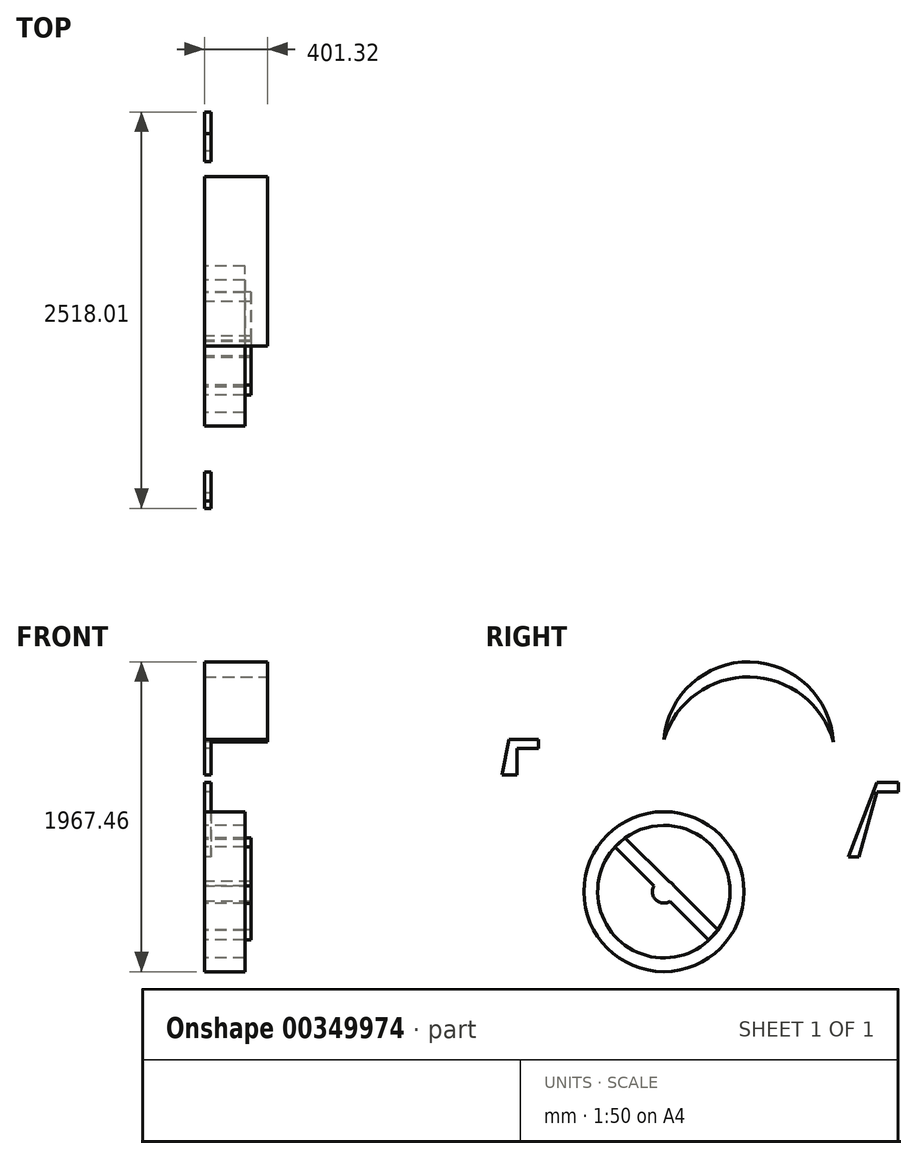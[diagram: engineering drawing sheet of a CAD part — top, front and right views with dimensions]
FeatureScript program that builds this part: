
annotation { "Feature Type Name" : "Feature", "Feature Type Description" : "" }
export const myFeature = defineFeature(function(context is Context, id is Id, definition is map)
    precondition{}
    {
        {
            var Q0;
            Q0=qCreatedBy(makeId("Right.planeOp"),FACE);
            var sketch = newSketch(context, id + "F0", { "sketchPlane" : qUnion([Q0])});
            skCircle(sketch, "E0", {"center": v(0, 0) * mm, "radius": 508 * mm});
            skCircle(sketch, "E1", {"center": v(0, 0) * mm, "radius": 420.64 * mm});
            skSolve(sketch);
        }
        {
            var Q0;
            Q0 = qSketchRegion(id + "F0", true);
            extrude(context, id + "F1", {"entities" : qUnion([Q0]), "depth" : 256.54 * mm});
        }
        {
            var Q0;
            Q0=qCreatedBy(makeId("Right.planeOp"),FACE);
            var sketch = newSketch(context, id + "F2", { "sketchPlane" : qUnion([Q0])});
            skCircle(sketch, "E2", {"center": v(0, 0) * mm, "radius": 73 * mm});
            skLineSegment(sketch, "E3", {"start": v(-310.82, 282.74) * mm, "end": v(282.74, -304.8) * mm});
            skLineSegment(sketch, "E4", {"start": v(282.74, -304.8) * mm, "end": v(343.63, -243.3) * mm});
            skLineSegment(sketch, "E5", {"start": v(343.63, -243.3) * mm, "end": v(-247.6, 341.94) * mm});
            skLineSegment(sketch, "E6", {"start": v(-247.6, 341.94) * mm, "end": v(-310.82, 282.74) * mm});
            skSolve(sketch);
        }
        {
            var Q0;
            Q0 = qSketchRegion(id + "F2", true);
            extrude(context, id + "F3", {"entities" : qUnion([Q0]), "operationType" : NewBodyOperationType.ADD, "depth" : 294.64 * mm});
        }
        {
            var Q0;
            Q0=qCreatedBy(makeId("Right.planeOp"),FACE);
            var sketch = newSketch(context, id + "F4", { "sketchPlane" : qUnion([Q0])});
            skArc(sketch, "E7", {"start": v(1076.69, 949.49) * mm, "mid": v(546.96, 1459.38) * mm, "end": v(0, 968.02) * mm});
            skLineSegment(sketch, "E8", {"start": v(0, 968.02) * mm, "end": v(1076.69, 949.49) * mm});
            skSolve(sketch);
        }
        {
            var Q0;
            Q0 = qSketchRegion(id + "F4", true);
            extrude(context, id + "F5", {"entities" : qUnion([Q0]), "depth" : 401.32 * mm, "offsetDistance" : 25.4 * mm});
        }
        {
            var Q0;
            Q0=makeQuery(id+"F5.opExtrude","CAP_FACE",FACE,{"disambiguationData":[OSD([sQuery(id+"F4.wireOp",EDGE,"E7"),sQuery(id+"F4.wireOp",EDGE,"E8")])],"isStart":false});
            var sketch = newSketch(context, id + "F6", { "sketchPlane" : qUnion([Q0])});
            skArc(sketch, "E9", {"start": v(1076.69, 949.49) * mm, "mid": v(545.32, 1363.83) * mm, "end": v(0, 968.02) * mm});
            skLineSegment(sketch, "E10", {"start": v(0, 968.02) * mm, "end": v(1076.69, 949.49) * mm});
            skSolve(sketch);
        }
        {
            var Q0;
            Q0 = qSketchRegion(id + "F6", true);
            extrude(context, id + "F7", {"entities" : qUnion([Q0]), "operationType" : NewBodyOperationType.REMOVE, "oppositeDirection" : true, "depth" : 815.34 * mm, "offsetDistance" : 25.4 * mm});
        }
        {
            var Q0;
            Q0=qCreatedBy(makeId("Right.planeOp"),FACE);
            var sketch = newSketch(context, id + "F8", { "sketchPlane" : qUnion([Q0])});
            skLineSegment(sketch, "E11", {"start": v(1352.13, 695.33) * mm, "end": v(1488.37, 695.33) * mm});
            skLineSegment(sketch, "E12", {"start": v(1488.37, 695.33) * mm, "end": v(1488.37, 633.8) * mm});
            skLineSegment(sketch, "E13", {"start": v(1488.37, 633.8) * mm, "end": v(1352.13, 633.8) * mm});
            skLineSegment(sketch, "E14", {"start": v(1352.13, 695.33) * mm, "end": v(1173.62, 219.73) * mm});
            skLineSegment(sketch, "E15", {"start": v(1173.62, 219.73) * mm, "end": v(1238.87, 219.73) * mm});
            skLineSegment(sketch, "E16", {"start": v(1238.87, 219.73) * mm, "end": v(1352.13, 633.8) * mm});
            skSolve(sketch);
        }
        {
            var Q0;
            Q0 = qSketchRegion(id + "F8", true);
            extrude(context, id + "F9", {"entities" : qUnion([Q0]), "depth" : 40.64 * mm, "offsetDistance" : 25.4 * mm});
        }
        {
            var Q0;
            Q0 = qSketchRegion(id + "F8", true);
            extrude(context, id + "F10", {"entities" : qUnion([Q0]), "operationType" : NewBodyOperationType.ADD, "depth" : 38.1 * mm, "offsetDistance" : 25.4 * mm});
        }
        {
            var Q0;
            Q0=qCreatedBy(makeId("Right.planeOp"),FACE);
            var sketch = newSketch(context, id + "F11", { "sketchPlane" : qUnion([Q0])});
            skLineSegment(sketch, "E17", {"start": v(-863.1, 966.95) * mm, "end": v(-983.47, 966.95) * mm});
            skLineSegment(sketch, "E18", {"start": v(-932.99, 908.7) * mm, "end": v(-797.08, 908.7) * mm});
            skLineSegment(sketch, "E19", {"start": v(-797.08, 908.7) * mm, "end": v(-797.08, 966.95) * mm});
            skLineSegment(sketch, "E20", {"start": v(-797.08, 966.95) * mm, "end": v(-863.1, 966.95) * mm});
            skLineSegment(sketch, "E21", {"start": v(-983.47, 966.95) * mm, "end": v(-1029.64, 739.88) * mm});
            skLineSegment(sketch, "E22", {"start": v(-1029.64, 739.88) * mm, "end": v(-932.99, 739.88) * mm});
            skLineSegment(sketch, "E23", {"start": v(-932.99, 739.88) * mm, "end": v(-932.99, 908.7) * mm});
            skSolve(sketch);
        }
        {
            var Q0;
            Q0 = qSketchRegion(id + "F11", true);
            extrude(context, id + "F12", {"entities" : qUnion([Q0]), "depth" : 40.64 * mm, "offsetDistance" : 25.4 * mm});
        }
    });
